# Revit family: SOT_Turano_Multiproduct_BIM_GB_R4311;R4312
name_source: partatom
category: Plumbing Fixtures
revit_build: Autodesk Revit MEP 2014 (Build: 20130308_1515(x64)
units: mm (PartAtom-declared; Revit-internal decimal feet)

## types (2) — shared parameters
Accessories = www.specifysottini.co.uk
AreaUnits = millimeters
Assembly Code = C1030200
AssetType = Fixed
BREEAM = No
Brand = Sottini
Color = White
Default Elevation = 800 mm
DurationUnit = year
ECA = No
ExpectedLife = 30
Finish = White
HandleMtl = SOT_Sottini_Fittings_Chrome_Render
IfcExportAs = IfcFurnitureType
IfcExportType = WORKTOP
InstallationInstructions = www.idealspec.co.uk/resources.html
LaminateMtl = SOT_Sottini_Laminate_White_Render
LinearUnits = millimeters
MainColor = White
ManufacturerURL = www.specifysottini.co.uk
Material = Laminated board
NBSDescription = Bathroom cupboards
NBSReference = 45-35-70/320
NominalDepth = 440 mm
NominalHeight = 120 mm  [stored 0.393701 ft]
ProductInformation = http://www.idealspec.co.uk
Shape = Rectangular
Space = Internal
SpareParts = www.fastpart-spares.co.uk
TMV3 = No
URL = www.specifysottini.co.uk
Uniclass2015Code = Pr_40_30_78_04
Uniclass2015Title = Bathroom Cupboard
Uniclass2015Version = Products v1.1
Version = 1
VolumeUnits = Litres
WRAS = No
WarrantyDescription = Manufacturers warranty
WarrantyDurationParts = 5
WarrantyDurationUnit = year
WaterEfficientProduct = No
zero-valued in all types: CWFU, Cost, HWFU, NominalLength, WFU

## per-type parameters (varying)
| type | BIMObjectName | Description | Features | Model | Name | NettWeight | NominalWidth | Size |
| R4311WG - Turano 800mm Shelf Unit | SOT_Sottini_Furniture_Turano_R4311WG | Turano 800mm shelf unit | Turano 800mm Shelf Unit | R4311WG | SOT_Furniture_Turano_R4311WG_Sottini | 5Kg | 797 mm | 440 x 797 x 120 mm |
| R4312WG - Turano 1000mm Shelf Unit | SOT_Sottini_Furniture_Turano_R4312WG | Turano 1000mm shelf unit | Turano 1000mm Shelf Unit | R4312WG | SOT_Furniture_Turano_R4312WG_Sottini | 5.5Kg | 997 mm | 440 x 997 x 120 mm |

note: [stored X ft] marks values corroborated as IEEE doubles in the binary element streams (Revit-internal decimal feet)

## geometry (parser evidence)
native form markers: Sweep x2
no freeform markers — native parametric forms only
